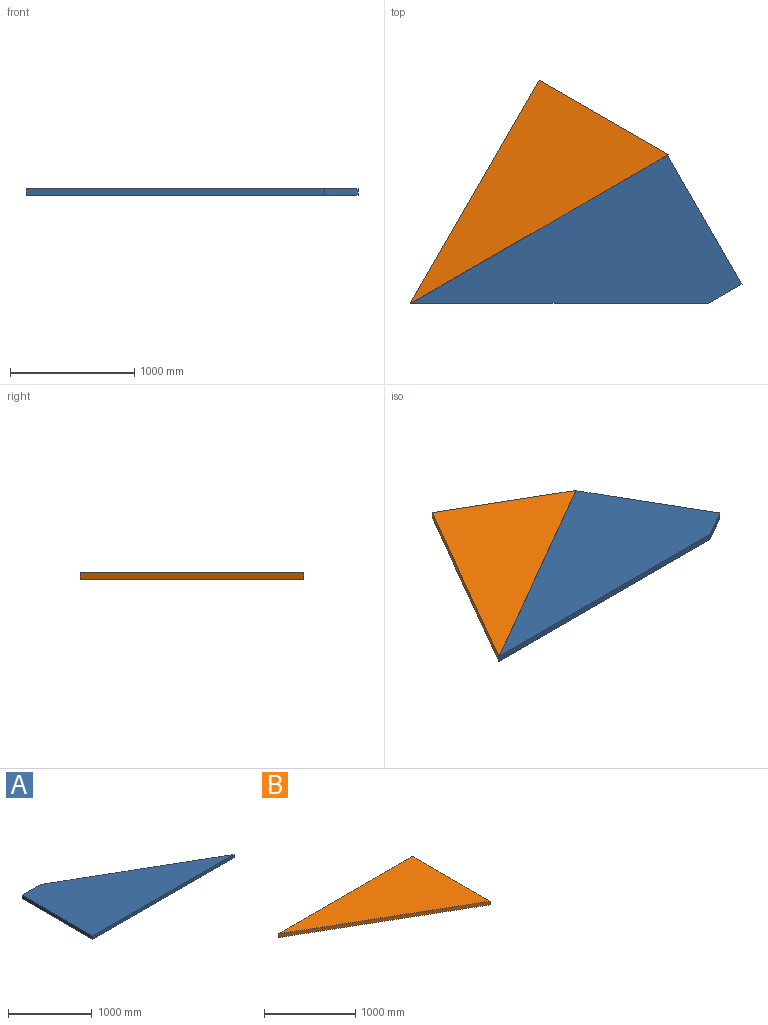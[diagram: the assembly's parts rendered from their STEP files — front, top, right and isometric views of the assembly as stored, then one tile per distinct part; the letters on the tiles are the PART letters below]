
ASSEMBLY  parts=2 mates=1
PART A: 6 faces, bbox 2390x1200x50 mm
  f0: plane 2390x50mm, normal (0,-1,0), area 119500mm2, adj f1,f3,f4,f5
  f1: plane 2078.46x1200mm, normal (0.5,0.87,0), area 120000mm2, adj f0,f2,f4,f5
  f2: plane 311.54x50mm, normal (0,1,0), area 15577mm2, adj f1,f3,f4,f5
  f3: plane 1200x50mm, normal (-1,0,0), area 60000mm2, adj f0,f2,f4,f5
  f4: plane 2390x1200mm, normal (0,0,1), area 1620923.4mm2, adj f0,f1,f2,f3
  f5: plane 2390x1200mm, normal (0,0,-1), area 1620923.4mm2, adj f0,f1,f2,f3
PART B: 5 faces, bbox 2078.5x1200x50 mm
  f0: plane 2078.46x1200mm, normal (-0.5,-0.87,0), area 120000mm2, adj f1,f2,f3,f4
  f1: plane 1200x50mm, normal (1,0,0), area 60000mm2, adj f0,f2,f3,f4
  f2: plane 2078.46x50mm, normal (0,1,0), area 103923mm2, adj f0,f1,f3,f4
  f3: plane 2078.46x1200mm, normal (0,0,1), area 1247076.6mm2, adj f0,f1,f2
  f4: plane 2078.46x1200mm, normal (0,0,-1), area 1247076.6mm2, adj f0,f1,f2
PLACE A rot(axis=(0,0,-1),150deg) t=(-1266.26,922.44,-498.07)mm
PLACE B rot(axis=(0,0,1),60deg) t=(202.02,1877.93,-498.07)mm
MATE fastened A.f0 <-> B.f0  axis (-0.5,0.87,0) through (-422.65,1525.19,-473.07)mm
